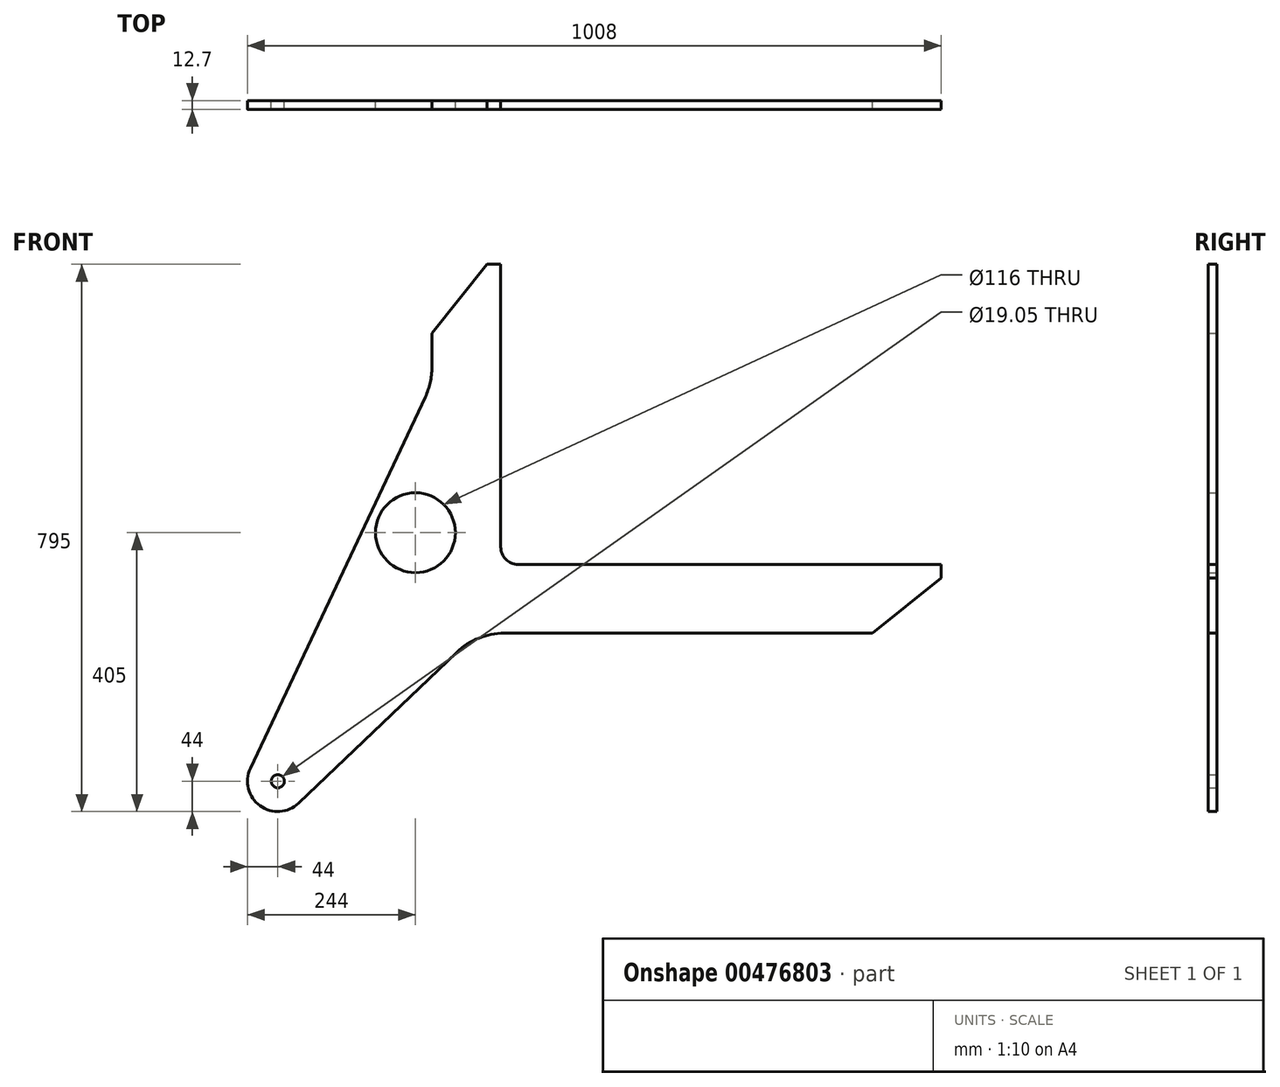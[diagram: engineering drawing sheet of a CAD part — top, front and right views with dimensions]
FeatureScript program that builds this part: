
annotation { "Feature Type Name" : "Feature", "Feature Type Description" : "" }
export const myFeature = defineFeature(function(context is Context, id is Id, definition is map)
    precondition{}
    {
        {
            var Q0;
            Q0=qCreatedBy(makeId("Front.planeOp"),FACE);
            var sketch = newSketch(context, id + "F0", { "sketchPlane" : qUnion([Q0])});
            skCircle(sketch, "E0", {"center": v(0, 0) * mm, "radius": 58 * mm});
            skCircle(sketch, "E1", {"center": v(-200, -361) * mm, "radius": 9.53 * mm});
            skArc(sketch, "E2", {"start": v(-239.8, -342.25) * mm, "mid": v(-225.73, -396.7) * mm, "end": v(-169.62, -392.83) * mm});
            skLineSegment(sketch, "E3", {"start": v(-169.62, -392.83) * mm, "end": v(59.95, -173.67) * mm});
            skLineSegment(sketch, "E4", {"start": v(129, -146) * mm, "end": v(664, -146) * mm});
            skLineSegment(sketch, "E5", {"start": v(664, -146) * mm, "end": v(764, -66) * mm});
            skLineSegment(sketch, "E6", {"start": v(764, -66) * mm, "end": v(764, -46) * mm});
            skLineSegment(sketch, "E7", {"start": v(764, -46) * mm, "end": v(149, -46) * mm});
            skLineSegment(sketch, "E8", {"start": v(124, -21) * mm, "end": v(124, 390) * mm});
            skLineSegment(sketch, "E9", {"start": v(124, 390) * mm, "end": v(104, 390) * mm});
            skLineSegment(sketch, "E10", {"start": v(104, 390) * mm, "end": v(24, 290) * mm});
            skLineSegment(sketch, "E11", {"start": v(24, 290) * mm, "end": v(24, 240) * mm});
            skLineSegment(sketch, "E12", {"start": v(14.46, 197.38) * mm, "end": v(-239.8, -342.25) * mm});
            skPoint(sketch, "E13.visualSharp", {"position": v(24, 217.62) * mm});
            skArc(sketch, "E13.filletArc", {"start": v(14.46, 197.38) * mm, "mid": v(21.59, 218.16) * mm, "end": v(24, 240) * mm});
            skPoint(sketch, "E14.visualSharp", {"position": v(88.93, -146) * mm});
            skArc(sketch, "E14.filletArc", {"start": v(129, -146) * mm, "mid": v(91.8, -153.17) * mm, "end": v(59.95, -173.67) * mm});
            skPoint(sketch, "E15.visualSharp", {"position": v(124, -46) * mm});
            skArc(sketch, "E15.filletArc", {"start": v(124, -21) * mm, "mid": v(131.32, -38.68) * mm, "end": v(149, -46) * mm});
            skSolve(sketch);
        }
        {
            var Q0;
            Q0=makeQuery(id+"F0.imprint","IMPRINT",FACE,{"disambiguationData":[TD([[makeQuery(id+"F0.imprint","IMPRINT",EDGE,{"derivedFrom":sQuery(id+"F0.wireOp",EDGE,"V7iE8r5z-8ez1-9WBL-U2KH-kt8EJKYPo8sT")}),-1.0]])]});
            var Q1;
            Q1=makeQuery(id+"F0.imprint","IMPRINT",FACE,{"disambiguationData":[TD([[makeQuery(id+"F0.imprint","IMPRINT",EDGE,{"derivedFrom":sQuery(id+"F0.wireOp",EDGE,"E0")}),-1.0]])]});
            extrude(context, id + "F1", {"entities" : qUnion([Q0, Q1]), "endBound" : BoundingType.SYMMETRIC, "depth" : (25.4 / 2) * mm});
        }
    });
